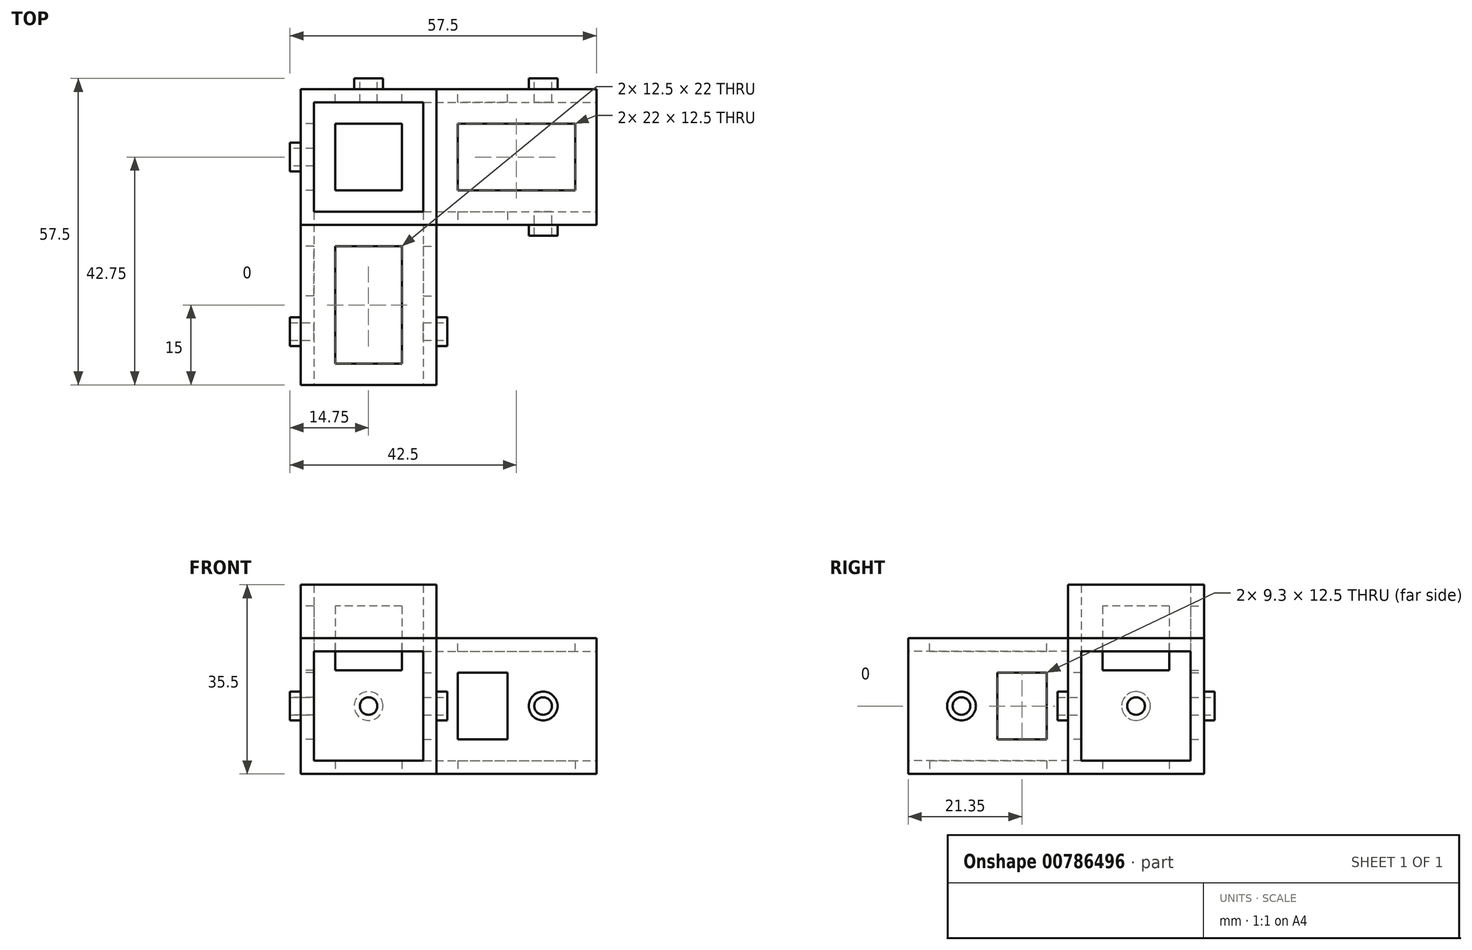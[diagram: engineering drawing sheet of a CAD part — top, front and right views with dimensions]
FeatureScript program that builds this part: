
annotation { "Feature Type Name" : "Feature", "Feature Type Description" : "" }
export const myFeature = defineFeature(function(context is Context, id is Id, definition is map)
    precondition{}
    {
        {
            var Q0;
            Q0=qCreatedBy(makeId("Top.planeOp"),FACE);
            var sketch = newSketch(context, id + "F0", { "sketchPlane" : qUnion([Q0])});
            skLineSegment(sketch, "E0.bottom", {"start": v(-10.25, 20.5) * mm, "end": v(10.25, 20.5) * mm});
            skLineSegment(sketch, "E0.top", {"start": v(-10.25, 0) * mm, "end": v(10.25, 0) * mm});
            skLineSegment(sketch, "E0.left", {"start": v(-10.25, 20.5) * mm, "end": v(-10.25, 0) * mm});
            skLineSegment(sketch, "E0.right", {"start": v(10.25, 20.5) * mm, "end": v(10.25, 0) * mm});
            skLineSegment(sketch, "E1.bottom", {"start": v(-12.75, 23) * mm, "end": v(12.75, 23) * mm});
            skLineSegment(sketch, "E1.top", {"start": v(-12.75, -2.5) * mm, "end": v(12.75, -2.5) * mm});
            skLineSegment(sketch, "E1.left", {"start": v(-12.75, 23) * mm, "end": v(-12.75, -2.5) * mm});
            skLineSegment(sketch, "E1.right", {"start": v(12.75, 23) * mm, "end": v(12.75, -2.5) * mm});
            skSolve(sketch);
        }
        {
            var Q0;
            Q0=makeQuery(id+"F0.imprint","IMPRINT",FACE,{"disambiguationData":[TD([[makeQuery(id+"F0.imprint","IMPRINT",EDGE,{"derivedFrom":sQuery(id+"F0.wireOp",EDGE,"E0.bottom")}),1.0]])]});
            extrude(context, id + "F1", {"entities" : qUnion([Q0]), "depth" : 35.5 * mm, "offsetDistance" : 25 * mm});
        }
        {
            var Q0;
            Q0=makeQuery(id+"F1.opExtrude","SWEPT_FACE",FACE,{"disambiguationData":[OSD([sQuery(id+"F0.wireOp",EDGE,"E1.top")])]});
            var sketch = newSketch(context, id + "F2", { "sketchPlane" : qUnion([Q0])});
            skLineSegment(sketch, "E2.bottom", {"start": v(-12.75, 0) * mm, "end": v(12.75, 0) * mm});
            skLineSegment(sketch, "E2.top", {"start": v(-12.75, 25.5) * mm, "end": v(12.75, 25.5) * mm});
            skLineSegment(sketch, "E2.left", {"start": v(-12.75, 0) * mm, "end": v(-12.75, 25.5) * mm});
            skLineSegment(sketch, "E2.right", {"start": v(12.75, 0) * mm, "end": v(12.75, 25.5) * mm});
            skSolve(sketch);
        }
        {
            var Q0;
            Q0=qSketchRegion(id+"F2",true);
            extrude(context, id + "F3", {"entities" : qUnion([Q0]), "operationType" : NewBodyOperationType.ADD, "depth" : 30 * mm, "offsetDistance" : 25 * mm});
        }
        {
            var Q0;
            Q0=qSketchRegion(id+"F2",true);
            extrude(context, id + "F4", {"entities" : qUnion([Q0]), "operationType" : NewBodyOperationType.ADD, "depth" : 10 * mm, "offsetDistance" : 25 * mm});
        }
        {
            var Q0;
            Q0=makeQuery(id+"F3.opExtrude","CAP_FACE",FACE,{"disambiguationData":[OSD([sQuery(id+"F2.wireOp",EDGE,"E2.bottom"),sQuery(id+"F2.wireOp",EDGE,"E2.top"),sQuery(id+"F2.wireOp",EDGE,"E2.left"),sQuery(id+"F2.wireOp",EDGE,"E2.right")])],"isStart":false});
            var sketch = newSketch(context, id + "F5", { "sketchPlane" : qUnion([Q0])});
            skLineSegment(sketch, "E3.bottom", {"start": v(-10.25, 2.5) * mm, "end": v(10.25, 2.5) * mm});
            skLineSegment(sketch, "E3.top", {"start": v(-10.25, 23) * mm, "end": v(10.25, 23) * mm});
            skLineSegment(sketch, "E3.left", {"start": v(-10.25, 2.5) * mm, "end": v(-10.25, 23) * mm});
            skLineSegment(sketch, "E3.right", {"start": v(10.25, 2.5) * mm, "end": v(10.25, 23) * mm});
            skSolve(sketch);
        }
        {
            var Q0;
            Q0=makeQuery(id+"F5.imprint","IMPRINT",FACE,{"disambiguationData":[TD([[makeQuery(id+"F5.imprint","IMPRINT",EDGE,{"derivedFrom":sQuery(id+"F5.wireOp",EDGE,"E3.bottom")}),1.0]])]});
            extrude(context, id + "F6", {"entities" : qUnion([Q0]), "operationType" : NewBodyOperationType.REMOVE, "oppositeDirection" : true, "depth" : 32.5 * mm, "offsetDistance" : 25 * mm});
        }
        {
            var Q0;
            Q0=makeQuery(id+"F3.boolean.opBoolean","MERGE",FACE,{"derivedFrom":[makeQuery(id+"F1.opExtrude","CAP_FACE",FACE,{"disambiguationData":[OSD([sQuery(id+"F0.wireOp",EDGE,"E0.bottom"),sQuery(id+"F0.wireOp",EDGE,"E0.top"),sQuery(id+"F0.wireOp",EDGE,"E0.left"),sQuery(id+"F0.wireOp",EDGE,"E0.right"),sQuery(id+"F0.wireOp",EDGE,"E1.bottom"),sQuery(id+"F0.wireOp",EDGE,"E1.top"),sQuery(id+"F0.wireOp",EDGE,"E1.left"),sQuery(id+"F0.wireOp",EDGE,"E1.right")])],"isStart":true}),makeQuery(id+"F3.opExtrude","SWEPT_FACE",FACE,{"disambiguationData":[OSD([sQuery(id+"F2.wireOp",EDGE,"E2.bottom")])]})]});
            var sketch = newSketch(context, id + "F7", { "sketchPlane" : qUnion([Q0])});
            skLineSegment(sketch, "E4.bottom", {"start": v(10.25, -20.5) * mm, "end": v(-10.25, -20.5) * mm});
            skLineSegment(sketch, "E4.top", {"start": v(10.25, 0) * mm, "end": v(-10.25, 0) * mm});
            skLineSegment(sketch, "E4.left", {"start": v(10.25, -20.5) * mm, "end": v(10.25, 0) * mm});
            skLineSegment(sketch, "E4.right", {"start": v(-10.25, -20.5) * mm, "end": v(-10.25, 0) * mm});
            skSolve(sketch);
        }
        {
            var Q0;
            Q0=qSketchRegion(id+"F7",true);
            extrude(context, id + "F8", {"entities" : qUnion([Q0]), "operationType" : NewBodyOperationType.ADD, "oppositeDirection" : true, "depth" : 2.5 * mm, "offsetDistance" : 25 * mm});
        }
        {
            var Q0;
            Q0=makeQuery(id+"F3.boolean.opBoolean","MERGE",FACE,{"derivedFrom":[makeQuery(id+"F1.opExtrude","SWEPT_FACE",FACE,{"disambiguationData":[OSD([sQuery(id+"F0.wireOp",EDGE,"E1.right")])]}),makeQuery(id+"F3.opExtrude","SWEPT_FACE",FACE,{"disambiguationData":[OSD([sQuery(id+"F2.wireOp",EDGE,"E2.right")])]})]});
            var sketch = newSketch(context, id + "F9", { "sketchPlane" : qUnion([Q0])});
            skLineSegment(sketch, "E5.bottom", {"start": v(-2.5, 25.5) * mm, "end": v(23, 25.5) * mm});
            skLineSegment(sketch, "E5.top", {"start": v(-2.5, 0) * mm, "end": v(23, 0) * mm});
            skLineSegment(sketch, "E5.left", {"start": v(-2.5, 25.5) * mm, "end": v(-2.5, 0) * mm});
            skLineSegment(sketch, "E5.right", {"start": v(23, 25.5) * mm, "end": v(23, 0) * mm});
            skSolve(sketch);
        }
        {
            var Q0;
            Q0 = qSketchRegion(id + "F9", true);
            extrude(context, id + "F10", {"entities" : qUnion([Q0]), "operationType" : NewBodyOperationType.ADD, "depth" : 30 * mm, "offsetDistance" : 25 * mm});
        }
        {
            var Q0;
            Q0=makeQuery(id+"F10.opExtrude","CAP_FACE",FACE,{"disambiguationData":[OSD([sQuery(id+"F9.wireOp",EDGE,"E5.bottom"),sQuery(id+"F9.wireOp",EDGE,"E5.top"),sQuery(id+"F9.wireOp",EDGE,"E5.left"),sQuery(id+"F9.wireOp",EDGE,"E5.right")])],"isStart":false});
            var sketch = newSketch(context, id + "F11", { "sketchPlane" : qUnion([Q0])});
            skLineSegment(sketch, "E6.bottom", {"start": v(0, 2.5) * mm, "end": v(20.5, 2.5) * mm});
            skLineSegment(sketch, "E6.top", {"start": v(0, 23) * mm, "end": v(20.5, 23) * mm});
            skLineSegment(sketch, "E6.left", {"start": v(0, 2.5) * mm, "end": v(0, 23) * mm});
            skLineSegment(sketch, "E6.right", {"start": v(20.5, 2.5) * mm, "end": v(20.5, 23) * mm});
            skSolve(sketch);
        }
        {
            var Q0;
            Q0 = qSketchRegion(id + "F11", true);
            extrude(context, id + "F12", {"entities" : qUnion([Q0]), "operationType" : NewBodyOperationType.REMOVE, "oppositeDirection" : true, "depth" : 32.5 * mm, "offsetDistance" : 25 * mm});
        }
        {
            var Q0;
            {var subQ0=sQuery(id+"F2.wireOp",EDGE,"E2.right");var subQ1=makeQuery(id+"F3.opExtrude","SWEPT_FACE",FACE,{"disambiguationData":[OSD([subQ0])]});var subQ2=sQuery(id+"F0.wireOp",EDGE,"E1.right");var subQ3=makeQuery(id+"F1.opExtrude","SWEPT_FACE",FACE,{"disambiguationData":[OSD([subQ2])]});var subQ6=sQuery(id+"F2.wireOp",EDGE,"E2.bottom");Q0=makeQuery(id+"F10.boolean.opBoolean","SPLIT",FACE,{"disambiguationData":[TD([makeQuery(id+"F3.opExtrude","SWEPT_FACE",FACE,{"disambiguationData":[OSD([subQ6])]})])],"derivedFrom":makeQuery(id+"F3.boolean.opBoolean","MERGE",FACE,{"derivedFrom":[subQ3,subQ1]})});}
            var sketch = newSketch(context, id + "F13", { "sketchPlane" : qUnion([Q0])});
            skCircle(sketch, "E7", {"center": v(-22.5, 12.75) * mm, "radius": 2.7 * mm});
            skSolve(sketch);
        }
        {
            var Q0;
            Q0 = qSketchRegion(id + "F13", true);
            extrude(context, id + "F14", {"entities" : qUnion([Q0]), "operationType" : NewBodyOperationType.ADD, "depth" : 2 * mm, "offsetDistance" : 25 * mm});
        }
        {
            var Q0;
            Q0=makeQuery(id+"F3.boolean.opBoolean","MERGE",FACE,{"derivedFrom":[makeQuery(id+"F1.opExtrude","SWEPT_FACE",FACE,{"disambiguationData":[OSD([sQuery(id+"F0.wireOp",EDGE,"E1.left")])]}),makeQuery(id+"F3.opExtrude","SWEPT_FACE",FACE,{"disambiguationData":[OSD([sQuery(id+"F2.wireOp",EDGE,"E2.left")])]})]});
            var sketch = newSketch(context, id + "F15", { "sketchPlane" : qUnion([Q0])});
            skCircle(sketch, "E8", {"center": v(22.5, 12.75) * mm, "radius": 2.7 * mm});
            skSolve(sketch);
        }
        {
            var Q0;
            Q0 = qSketchRegion(id + "F15", true);
            extrude(context, id + "F16", {"entities" : qUnion([Q0]), "operationType" : NewBodyOperationType.ADD, "depth" : 2 * mm, "offsetDistance" : 25 * mm});
        }
        {
            var Q0;
            Q0=makeQuery(id+"F14.opExtrude","CAP_FACE",FACE,{"disambiguationData":[OSD([sQuery(id+"F13.wireOp",EDGE,"E7")])],"isStart":false});
            var sketch = newSketch(context, id + "F17", { "sketchPlane" : qUnion([Q0])});
            skCircle(sketch, "E9", {"center": v(-22.5, 12.75) * mm, "radius": 1.65 * mm});
            skSolve(sketch);
        }
        {
            var Q0;
            Q0 = qSketchRegion(id + "F17", true);
            extrude(context, id + "F18", {"entities" : qUnion([Q0]), "operationType" : NewBodyOperationType.REMOVE, "oppositeDirection" : true, "depth" : 30 * mm, "offsetDistance" : 25 * mm});
        }
        {
            var Q0;
            Q0=makeQuery(id+"F10.opExtrude","SWEPT_FACE",FACE,{"disambiguationData":[OSD([sQuery(id+"F9.wireOp",EDGE,"E5.left")])]});
            var sketch = newSketch(context, id + "F19", { "sketchPlane" : qUnion([Q0])});
            skCircle(sketch, "E10", {"center": v(32.75, 12.75) * mm, "radius": 2.7 * mm});
            skSolve(sketch);
        }
        {
            var Q0;
            Q0 = qSketchRegion(id + "F19", true);
            extrude(context, id + "F20", {"entities" : qUnion([Q0]), "operationType" : NewBodyOperationType.ADD, "depth" : 2 * mm, "offsetDistance" : 25 * mm});
        }
        {
            var Q0;
            Q0=makeQuery(id+"F10.boolean.opBoolean","MERGE",FACE,{"derivedFrom":[makeQuery(id+"F1.opExtrude","SWEPT_FACE",FACE,{"disambiguationData":[OSD([sQuery(id+"F0.wireOp",EDGE,"E1.bottom")])]}),makeQuery(id+"F10.opExtrude","SWEPT_FACE",FACE,{"disambiguationData":[OSD([sQuery(id+"F9.wireOp",EDGE,"E5.right")])]})]});
            var sketch = newSketch(context, id + "F21", { "sketchPlane" : qUnion([Q0])});
            skCircle(sketch, "E11", {"center": v(-32.75, 12.75) * mm, "radius": 2.7 * mm});
            skSolve(sketch);
        }
        {
            var Q0;
            Q0 = qSketchRegion(id + "F21", true);
            extrude(context, id + "F22", {"entities" : qUnion([Q0]), "operationType" : NewBodyOperationType.ADD, "depth" : 2 * mm, "offsetDistance" : 25 * mm});
        }
        {
            var Q0;
            Q0=makeQuery(id+"F22.opExtrude","CAP_FACE",FACE,{"disambiguationData":[OSD([sQuery(id+"F21.wireOp",EDGE,"E11")])],"isStart":false});
            var sketch = newSketch(context, id + "F23", { "sketchPlane" : qUnion([Q0])});
            skCircle(sketch, "E12", {"center": v(-32.75, 12.75) * mm, "radius": 1.65 * mm});
            skSolve(sketch);
        }
        {
            var Q0;
            Q0 = qSketchRegion(id + "F23", true);
            extrude(context, id + "F24", {"entities" : qUnion([Q0]), "operationType" : NewBodyOperationType.REMOVE, "oppositeDirection" : true, "depth" : 30 * mm, "offsetDistance" : 25 * mm});
        }
        {
            var Q0;
            Q0=makeQuery(id+"F3.boolean.opBoolean","MERGE",FACE,{"derivedFrom":[makeQuery(id+"F1.opExtrude","SWEPT_FACE",FACE,{"disambiguationData":[OSD([sQuery(id+"F0.wireOp",EDGE,"E1.left")])]}),makeQuery(id+"F3.opExtrude","SWEPT_FACE",FACE,{"disambiguationData":[OSD([sQuery(id+"F2.wireOp",EDGE,"E2.left")])]})]});
            var sketch = newSketch(context, id + "F25", { "sketchPlane" : qUnion([Q0])});
            skCircle(sketch, "E13", {"center": v(-10.25, 12.75) * mm, "radius": 2.7 * mm});
            skSolve(sketch);
        }
        {
            var Q0;
            Q0 = qSketchRegion(id + "F25", true);
            extrude(context, id + "F26", {"entities" : qUnion([Q0]), "operationType" : NewBodyOperationType.ADD, "depth" : 2 * mm, "offsetDistance" : 25 * mm});
        }
        {
            var Q0;
            Q0=makeQuery(id+"F26.opExtrude","CAP_FACE",FACE,{"disambiguationData":[OSD([sQuery(id+"F25.wireOp",EDGE,"E13")])],"isStart":false});
            var sketch = newSketch(context, id + "F27", { "sketchPlane" : qUnion([Q0])});
            skCircle(sketch, "E14", {"center": v(-10.25, 12.75) * mm, "radius": 1.65 * mm});
            skSolve(sketch);
        }
        {
            var Q0;
            Q0 = qSketchRegion(id + "F27", true);
            extrude(context, id + "F28", {"entities" : qUnion([Q0]), "operationType" : NewBodyOperationType.REMOVE, "oppositeDirection" : true, "depth" : 25 * mm, "offsetDistance" : 25 * mm});
        }
        {
            var Q0;
            Q0=makeQuery(id+"F10.boolean.opBoolean","MERGE",FACE,{"derivedFrom":[makeQuery(id+"F1.opExtrude","SWEPT_FACE",FACE,{"disambiguationData":[OSD([sQuery(id+"F0.wireOp",EDGE,"E1.bottom")])]}),makeQuery(id+"F10.opExtrude","SWEPT_FACE",FACE,{"disambiguationData":[OSD([sQuery(id+"F9.wireOp",EDGE,"E5.right")])]})]});
            var sketch = newSketch(context, id + "F29", { "sketchPlane" : qUnion([Q0])});
            skCircle(sketch, "E15", {"center": v(0, 12.75) * mm, "radius": 2.7 * mm});
            skSolve(sketch);
        }
        {
            var Q0;
            Q0 = qSketchRegion(id + "F29", true);
            extrude(context, id + "F30", {"entities" : qUnion([Q0]), "operationType" : NewBodyOperationType.ADD, "depth" : 2 * mm, "offsetDistance" : 25 * mm});
        }
        {
            var Q0;
            Q0=makeQuery(id+"F30.opExtrude","CAP_FACE",FACE,{"disambiguationData":[OSD([sQuery(id+"F29.wireOp",EDGE,"E15")])],"isStart":false});
            var sketch = newSketch(context, id + "F31", { "sketchPlane" : qUnion([Q0])});
            skCircle(sketch, "E16", {"center": v(0, 12.75) * mm, "radius": 1.65 * mm});
            skSolve(sketch);
        }
        {
            var Q0;
            Q0 = qSketchRegion(id + "F31", true);
            extrude(context, id + "F32", {"entities" : qUnion([Q0]), "operationType" : NewBodyOperationType.REMOVE, "oppositeDirection" : true, "depth" : 25 * mm, "offsetDistance" : 25 * mm});
        }
        {
            var Q0;
            Q0=makeQuery(id+"F10.boolean.opBoolean","MERGE",FACE,{"derivedFrom":[makeQuery(id+"F8.boolean.opBoolean","MERGE",FACE,{"derivedFrom":[makeQuery(id+"F3.boolean.opBoolean","MERGE",FACE,{"derivedFrom":[makeQuery(id+"F1.opExtrude","CAP_FACE",FACE,{"disambiguationData":[OSD([sQuery(id+"F0.wireOp",EDGE,"E0.bottom"),sQuery(id+"F0.wireOp",EDGE,"E0.top"),sQuery(id+"F0.wireOp",EDGE,"E0.left"),sQuery(id+"F0.wireOp",EDGE,"E0.right"),sQuery(id+"F0.wireOp",EDGE,"E1.bottom"),sQuery(id+"F0.wireOp",EDGE,"E1.top"),sQuery(id+"F0.wireOp",EDGE,"E1.left"),sQuery(id+"F0.wireOp",EDGE,"E1.right")])],"isStart":true}),makeQuery(id+"F3.opExtrude","SWEPT_FACE",FACE,{"disambiguationData":[OSD([sQuery(id+"F2.wireOp",EDGE,"E2.bottom")])]})]}),makeQuery(id+"F8.opExtrude","CAP_FACE",FACE,{"disambiguationData":[OSD([sQuery(id+"F7.wireOp",EDGE,"E4.bottom"),sQuery(id+"F7.wireOp",EDGE,"E4.top"),sQuery(id+"F7.wireOp",EDGE,"E4.left"),sQuery(id+"F7.wireOp",EDGE,"E4.right")])],"isStart":true})]}),makeQuery(id+"F10.opExtrude","SWEPT_FACE",FACE,{"disambiguationData":[OSD([sQuery(id+"F9.wireOp",EDGE,"E5.top")])]})]});
            var sketch = newSketch(context, id + "F33", { "sketchPlane" : qUnion([Q0])});
            skLineSegment(sketch, "E17.bottom", {"start": v(-6.25, 28.5) * mm, "end": v(6.25, 28.5) * mm});
            skLineSegment(sketch, "E17.top", {"start": v(-6.25, 6.5) * mm, "end": v(6.25, 6.5) * mm});
            skLineSegment(sketch, "E17.left", {"start": v(-6.25, 28.5) * mm, "end": v(-6.25, 6.5) * mm});
            skLineSegment(sketch, "E17.right", {"start": v(6.25, 28.5) * mm, "end": v(6.25, 6.5) * mm});
            skLineSegment(sketch, "E18.bottom", {"start": v(-6.25, -4) * mm, "end": v(6.25, -4) * mm});
            skLineSegment(sketch, "E18.top", {"start": v(-6.25, -16.5) * mm, "end": v(6.25, -16.5) * mm});
            skLineSegment(sketch, "E18.left", {"start": v(-6.25, -4) * mm, "end": v(-6.25, -16.5) * mm});
            skLineSegment(sketch, "E18.right", {"start": v(6.25, -4) * mm, "end": v(6.25, -16.5) * mm});
            skLineSegment(sketch, "E19.bottom", {"start": v(16.75, -4) * mm, "end": v(38.75, -4) * mm});
            skLineSegment(sketch, "E19.top", {"start": v(16.75, -16.5) * mm, "end": v(38.75, -16.5) * mm});
            skLineSegment(sketch, "E19.left", {"start": v(16.75, -4) * mm, "end": v(16.75, -16.5) * mm});
            skLineSegment(sketch, "E19.right", {"start": v(38.75, -4) * mm, "end": v(38.75, -16.5) * mm});
            skSolve(sketch);
        }
        {
            var Q0;
            Q0=makeQuery(id+"F33.imprint","IMPRINT",FACE,{"disambiguationData":[TD([[makeQuery(id+"F33.imprint","IMPRINT",EDGE,{"derivedFrom":sQuery(id+"F33.wireOp",EDGE,"E19.bottom")}),-1.0]])]});
            var Q1;
            Q1=makeQuery(id+"F33.imprint","IMPRINT",FACE,{"disambiguationData":[TD([[makeQuery(id+"F33.imprint","IMPRINT",EDGE,{"derivedFrom":sQuery(id+"F33.wireOp",EDGE,"E18.bottom")}),-1.0]])]});
            var Q2;
            Q2=makeQuery(id+"F33.imprint","IMPRINT",FACE,{"disambiguationData":[TD([[makeQuery(id+"F33.imprint","IMPRINT",EDGE,{"derivedFrom":sQuery(id+"F33.wireOp",EDGE,"E17.bottom")}),-1.0]])]});
            extrude(context, id + "F34", {"entities" : qUnion([Q0, Q1, Q2]), "operationType" : NewBodyOperationType.REMOVE, "oppositeDirection" : true, "depth" : 2.5 * mm, "offsetDistance" : 25 * mm});
        }
        {
            var Q0;
            {var subQ0=sQuery(id+"F2.wireOp",EDGE,"E2.right");var subQ1=makeQuery(id+"F3.opExtrude","SWEPT_FACE",FACE,{"disambiguationData":[OSD([subQ0])]});var subQ2=sQuery(id+"F0.wireOp",EDGE,"E1.right");var subQ3=makeQuery(id+"F1.opExtrude","SWEPT_FACE",FACE,{"disambiguationData":[OSD([subQ2])]});var subQ6=sQuery(id+"F2.wireOp",EDGE,"E2.bottom");Q0=makeQuery(id+"F10.boolean.opBoolean","SPLIT",FACE,{"disambiguationData":[TD([makeQuery(id+"F3.opExtrude","SWEPT_FACE",FACE,{"disambiguationData":[OSD([subQ6])]})])],"derivedFrom":makeQuery(id+"F3.boolean.opBoolean","MERGE",FACE,{"derivedFrom":[subQ3,subQ1]})});}
            var sketch = newSketch(context, id + "F35", { "sketchPlane" : qUnion([Q0])});
            skLineSegment(sketch, "E20.bottom", {"start": v(-6.5, 19) * mm, "end": v(-15.8, 19) * mm});
            skLineSegment(sketch, "E20.top", {"start": v(-6.5, 6.5) * mm, "end": v(-15.8, 6.5) * mm});
            skLineSegment(sketch, "E20.left", {"start": v(-6.5, 19) * mm, "end": v(-6.5, 6.5) * mm});
            skLineSegment(sketch, "E20.right", {"start": v(-15.8, 19) * mm, "end": v(-15.8, 6.5) * mm});
            skSolve(sketch);
        }
        {
            var Q0;
            Q0 = qSketchRegion(id + "F35", true);
            extrude(context, id + "F36", {"entities" : qUnion([Q0]), "operationType" : NewBodyOperationType.REMOVE, "oppositeDirection" : true, "depth" : 2.5 * mm, "offsetDistance" : 25 * mm});
        }
        {
            var Q0;
            Q0=makeQuery(id+"F3.boolean.opBoolean","MERGE",FACE,{"derivedFrom":[makeQuery(id+"F1.opExtrude","SWEPT_FACE",FACE,{"disambiguationData":[OSD([sQuery(id+"F0.wireOp",EDGE,"E1.left")])]}),makeQuery(id+"F3.opExtrude","SWEPT_FACE",FACE,{"disambiguationData":[OSD([sQuery(id+"F2.wireOp",EDGE,"E2.left")])]})]});
            var sketch = newSketch(context, id + "F37", { "sketchPlane" : qUnion([Q0])});
            skLineSegment(sketch, "E21.bottom", {"start": v(15.8, 19) * mm, "end": v(6.5, 19) * mm});
            skLineSegment(sketch, "E21.top", {"start": v(15.8, 6.5) * mm, "end": v(6.5, 6.5) * mm});
            skLineSegment(sketch, "E21.left", {"start": v(15.8, 19) * mm, "end": v(15.8, 6.5) * mm});
            skLineSegment(sketch, "E21.right", {"start": v(6.5, 19) * mm, "end": v(6.5, 6.5) * mm});
            skLineSegment(sketch, "E22.bottom", {"start": v(-16.5, 31.5) * mm, "end": v(-4, 31.5) * mm});
            skLineSegment(sketch, "E22.top", {"start": v(-16.5, 19.45) * mm, "end": v(-4, 19.45) * mm});
            skLineSegment(sketch, "E22.left", {"start": v(-16.5, 31.5) * mm, "end": v(-16.5, 19.45) * mm});
            skLineSegment(sketch, "E22.right", {"start": v(-4, 31.5) * mm, "end": v(-4, 19.45) * mm});
            skSolve(sketch);
        }
        {
            var Q0;
            Q0 = qSketchRegion(id + "F37", true);
            extrude(context, id + "F38", {"entities" : qUnion([Q0]), "operationType" : NewBodyOperationType.REMOVE, "oppositeDirection" : true, "depth" : 2.5 * mm, "offsetDistance" : 25 * mm});
        }
        {
            var Q0;
            Q0=makeQuery(id+"F10.boolean.opBoolean","MERGE",FACE,{"derivedFrom":[makeQuery(id+"F1.opExtrude","SWEPT_FACE",FACE,{"disambiguationData":[OSD([sQuery(id+"F0.wireOp",EDGE,"E1.bottom")])]}),makeQuery(id+"F10.opExtrude","SWEPT_FACE",FACE,{"disambiguationData":[OSD([sQuery(id+"F9.wireOp",EDGE,"E5.right")])]})]});
            var sketch = newSketch(context, id + "F39", { "sketchPlane" : qUnion([Q0])});
            skLineSegment(sketch, "E23.bottom", {"start": v(-26.05, 19) * mm, "end": v(-16.75, 19) * mm});
            skLineSegment(sketch, "E23.top", {"start": v(-26.05, 6.5) * mm, "end": v(-16.75, 6.5) * mm});
            skLineSegment(sketch, "E23.left", {"start": v(-26.05, 19) * mm, "end": v(-26.05, 6.5) * mm});
            skLineSegment(sketch, "E23.right", {"start": v(-16.75, 19) * mm, "end": v(-16.75, 6.5) * mm});
            skLineSegment(sketch, "E24.bottom", {"start": v(-6.25, 31.5) * mm, "end": v(6.25, 31.5) * mm});
            skLineSegment(sketch, "E24.top", {"start": v(-6.25, 19.45) * mm, "end": v(6.25, 19.45) * mm});
            skLineSegment(sketch, "E24.left", {"start": v(-6.25, 31.5) * mm, "end": v(-6.25, 19.45) * mm});
            skLineSegment(sketch, "E24.right", {"start": v(6.25, 31.5) * mm, "end": v(6.25, 19.45) * mm});
            skSolve(sketch);
        }
        {
            var Q0;
            Q0 = qSketchRegion(id + "F39", true);
            extrude(context, id + "F40", {"entities" : qUnion([Q0]), "operationType" : NewBodyOperationType.REMOVE, "oppositeDirection" : true, "depth" : 2.5 * mm, "offsetDistance" : 25 * mm});
        }
        {
            var Q0;
            Q0=makeQuery(id+"F10.opExtrude","SWEPT_FACE",FACE,{"disambiguationData":[OSD([sQuery(id+"F9.wireOp",EDGE,"E5.bottom")])]});
            var sketch = newSketch(context, id + "F41", { "sketchPlane" : qUnion([Q0])});
            skLineSegment(sketch, "E25.bottom", {"start": v(16.75, 4) * mm, "end": v(38.75, 4) * mm});
            skLineSegment(sketch, "E25.top", {"start": v(16.75, 16.5) * mm, "end": v(38.75, 16.5) * mm});
            skLineSegment(sketch, "E25.left", {"start": v(16.75, 4) * mm, "end": v(16.75, 16.5) * mm});
            skLineSegment(sketch, "E25.right", {"start": v(38.75, 4) * mm, "end": v(38.75, 16.5) * mm});
            skLineSegment(sketch, "E26.bottom", {"start": v(-6.25, -28.5) * mm, "end": v(6.25, -28.5) * mm});
            skLineSegment(sketch, "E26.top", {"start": v(-6.25, -6.5) * mm, "end": v(6.25, -6.5) * mm});
            skLineSegment(sketch, "E26.left", {"start": v(-6.25, -28.5) * mm, "end": v(-6.25, -6.5) * mm});
            skLineSegment(sketch, "E26.right", {"start": v(6.25, -28.5) * mm, "end": v(6.25, -6.5) * mm});
            skSolve(sketch);
        }
        {
            var Q0;
            Q0 = qSketchRegion(id + "F41", true);
            extrude(context, id + "F42", {"entities" : qUnion([Q0]), "operationType" : NewBodyOperationType.REMOVE, "oppositeDirection" : true, "depth" : 2.5 * mm, "offsetDistance" : 25 * mm});
        }
        {
            var Q0;
            Q0=makeQuery(id+"F10.opExtrude","SWEPT_FACE",FACE,{"disambiguationData":[OSD([sQuery(id+"F9.wireOp",EDGE,"E5.left")])]});
            var sketch = newSketch(context, id + "F43", { "sketchPlane" : qUnion([Q0])});
            skLineSegment(sketch, "E27.bottom", {"start": v(16.75, 19) * mm, "end": v(26.05, 19) * mm});
            skLineSegment(sketch, "E27.top", {"start": v(16.75, 6.5) * mm, "end": v(26.05, 6.5) * mm});
            skLineSegment(sketch, "E27.left", {"start": v(16.75, 19) * mm, "end": v(16.75, 6.5) * mm});
            skLineSegment(sketch, "E27.right", {"start": v(26.05, 19) * mm, "end": v(26.05, 6.5) * mm});
            skSolve(sketch);
        }
        {
            var Q0;
            Q0 = qSketchRegion(id + "F43", true);
            extrude(context, id + "F44", {"entities" : qUnion([Q0]), "operationType" : NewBodyOperationType.REMOVE, "oppositeDirection" : true, "depth" : 2.5 * mm, "offsetDistance" : 25 * mm});
        }
    });
